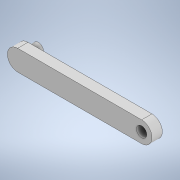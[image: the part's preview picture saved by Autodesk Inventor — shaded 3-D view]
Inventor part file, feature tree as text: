
AUTODESK INVENTOR PART (.ipt)
format: ipt  version: 2022 (Build 260153000, 153)  size: 107,008 bytes
history: native  units: mm
features: extrude x2, sketch x1
ambient origin geometry x8: Origin, YZ Plane, XZ Plane, XY Plane, X Axis, Y Axis, Z Axis, Center Point
bodies: Solid1 (feature_tree)
feature tree (3):
  sketch  "Sketch1"  dims[d0=60.0mm d1=10.0mm d2=5.0mm d3=5.0mm d4=0.0mm d5=5.0mm d6=0.0mm]
  extrude  "Extrusion1"  Depth=10.0mm
  extrude  "Extrusion2"  Depth=5.0mm
